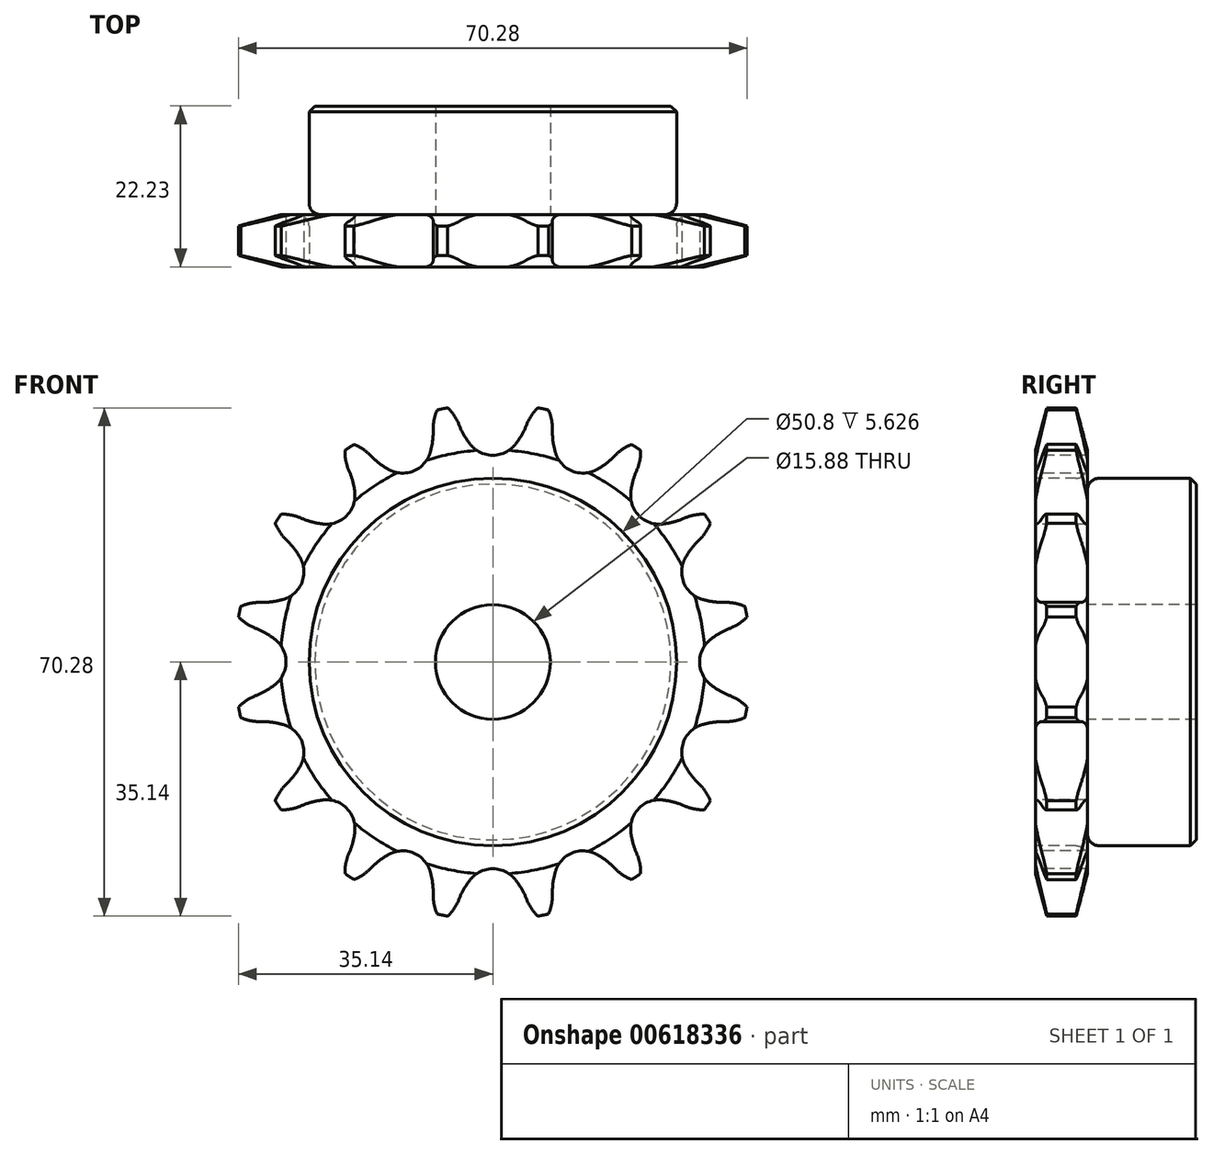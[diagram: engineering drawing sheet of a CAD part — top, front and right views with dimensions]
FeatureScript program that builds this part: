
annotation { "Feature Type Name" : "Feature", "Feature Type Description" : "" }
export const myFeature = defineFeature(function(context is Context, id is Id, definition is map)
    precondition{}
    {
        {
            var Q0;
            Q0=qCreatedBy(makeId("Right.planeOp"),FACE);
            var sketch = newSketch(context, id + "F0", { "sketchPlane" : qUnion([Q0])});
            skLineSegment(sketch, "E0", {"start": v(0, 0) * mm, "end": v(26.74, 0) * mm, "construction": true});
            skLineSegment(sketch, "E1.bottom", {"start": v(0, 7.94) * mm, "end": v(7.21, 7.94) * mm});
            skLineSegment(sketch, "E1.top", {"start": v(0, 35.69) * mm, "end": v(7.21, 35.69) * mm});
            skLineSegment(sketch, "E1.left", {"start": v(0, 7.94) * mm, "end": v(0, 35.69) * mm});
            skLineSegment(sketch, "E1.right", {"start": v(7.21, 7.94) * mm, "end": v(7.21, 35.69) * mm});
            skLineSegment(sketch, "E2.bottom", {"start": v(0, 7.94) * mm, "end": v(22.23, 7.94) * mm});
            skLineSegment(sketch, "E2.top", {"start": v(0, 25.4) * mm, "end": v(22.23, 25.4) * mm});
            skLineSegment(sketch, "E2.left", {"start": v(0, 7.94) * mm, "end": v(0, 25.4) * mm});
            skLineSegment(sketch, "E2.right", {"start": v(22.23, 7.94) * mm, "end": v(22.22, 25.4) * mm});
            skLineSegment(sketch, "E3.MirrorCS", {"start": v(0, -7.94) * mm, "end": v(7.21, -7.94) * mm});
            skLineSegment(sketch, "E4.MirrorCS", {"start": v(22.23, -7.94) * mm, "end": v(22.23, -25.4) * mm});
            skLineSegment(sketch, "E5.MirrorCS", {"start": v(0, -7.94) * mm, "end": v(0, -25.4) * mm});
            skLineSegment(sketch, "E6.MirrorCS", {"start": v(0, -35.69) * mm, "end": v(7.21, -35.69) * mm});
            skLineSegment(sketch, "E7.MirrorCS", {"start": v(0, -7.94) * mm, "end": v(0, -35.69) * mm});
            skLineSegment(sketch, "E8.MirrorCS", {"start": v(7.21, -7.94) * mm, "end": v(7.21, -35.69) * mm});
            skLineSegment(sketch, "E9.MirrorCS", {"start": v(0, -7.94) * mm, "end": v(22.23, -7.94) * mm});
            skLineSegment(sketch, "E10.MirrorCS", {"start": v(0, -25.4) * mm, "end": v(22.23, -25.4) * mm});
            skSolve(sketch);
        }
        {
            var Q0;
            {var subQ0=sQuery(id+"F0.wireOp",EDGE,"E1.top");Q0=makeQuery(id+"F0.imprint","IMPRINT",FACE,{"disambiguationData":[TD([[makeQuery(id+"F0.imprint","IMPRINT",EDGE,{"derivedFrom":subQ0}),-1.0]])]});}
            var Q1;
            {var subQ5=sQuery(id+"F0.wireOp",EDGE,"E2.left");Q1=makeQuery(id+"F0.imprint","IMPRINT",FACE,{"disambiguationData":[TD([[makeQuery(id+"F0.imprint","IMPRINT",EDGE,{"derivedFrom":subQ5}),-1.0]])]});}
            var Q2;
            {var subQ5=sQuery(id+"F0.wireOp",EDGE,"E2.right");Q2=makeQuery(id+"F0.imprint","IMPRINT",FACE,{"disambiguationData":[TD([[makeQuery(id+"F0.imprint","IMPRINT",EDGE,{"derivedFrom":subQ5}),1.0]])]});}
            var Q3;
            Q3=sQuery(id+"F0.wireOp",EDGE,"E0");
            revolve(context, id + "F1", {"entities" : qUnion([Q0, Q1, Q2]), "axis" : qUnion([Q3]), "revolveType" : RevolveType.FULL});
        }
        {
            var Q0;
            Q0=makeQuery(id+"F1.opRevolve","SWEPT_EDGE",EDGE,{"disambiguationData":[OSD([sQuery(id+"F0.wireOp",EDGE,"E1.right"),sQuery(id+"F0.wireOp",EDGE,"E2.top")])]});
            fillet(context, id + "F2", {"entities" : qUnion([Q0]), "radius" : 1.59 * mm, "tangentPropagation" : true, "allowEdgeOverflow" : false});
        }
        {
            var Q0;
            Q0=makeQuery(id+"F1.opRevolve","SWEPT_EDGE",EDGE,{"disambiguationData":[OSD([sQuery(id+"F0.wireOp",EDGE,"E2.top"),sQuery(id+"F0.wireOp",EDGE,"E2.right")])]});
            chamfer(context, id + "F3", {"entities" : qUnion([Q0]), "width" : 0.8 * mm, "tangentPropagation" : true});
        }
        {
            var Q0;
            Q0=makeQuery(id+"F1.opRevolve","SWEPT_FACE",FACE,{"disambiguationData":[OSD([sQuery(id+"F0.wireOp",EDGE,"E1.top")])]});
            chamfer(context, id + "F4", {"entities" : qUnion([Q0]), "chamferType" : ChamferType.TWO_OFFSETS, "width1" : 6.35 * mm, "oppositeDirection" : false, "width2" : 1.57 * mm, "tangentPropagation" : true});
        }
        {
            var Q0;
            Q0=makeQuery(id+"F1.opRevolve","SWEPT_FACE",FACE,{"disambiguationData":[OSD([sQuery(id+"F0.wireOp",EDGE,"E1.left"),sQuery(id+"F0.wireOp",EDGE,"E2.left")])]});
            var sketch = newSketch(context, id + "F5", { "sketchPlane" : qUnion([Q0])});
            skLineSegment(sketch, "E11", {"start": v(0, 0) * mm, "end": v(0, 32.55) * mm, "construction": true});
            skLineSegment(sketch, "E12", {"start": v(0, 32.55) * mm, "end": v(33.66, 32.55) * mm, "construction": true});
            skLineSegment(sketch, "E13", {"start": v(0, 32.55) * mm, "end": v(5, 36.56) * mm, "construction": true});
            skLineSegment(sketch, "E14", {"start": v(5, 36.56) * mm, "end": v(-3.9, 32.55) * mm, "construction": true});
            skLineSegment(sketch, "E15", {"start": v(3.62, 15.85) * mm, "end": v(-3.9, 32.55) * mm, "construction": true});
            skArc(sketch, "E16", {"start": v(-7.13, 35.87) * mm, "mid": v(-15.94, 26.26) * mm, "end": v(-4.66, 32.79) * mm, "construction": true});
            skArc(sketch, "E17", {"start": v(-4.66, 32.79) * mm, "mid": v(-5.66, 34.52) * mm, "end": v(-7.13, 35.87) * mm});
            skLineSegment(sketch, "E18", {"start": v(-4.66, 32.79) * mm, "end": v(-4.66, 32.79) * mm});
            skArc(sketch, "E19", {"start": v(-3.1, 30.07) * mm, "mid": v(-1.71, 28.98) * mm, "end": v(0, 28.59) * mm});
            skArc(sketch, "E20", {"start": v(-4.66, 32.79) * mm, "mid": v(-3.98, 31.37) * mm, "end": v(-3.1, 30.07) * mm});
            skArc(sketch, "E21.MirrorCS", {"start": v(4.66, 32.79) * mm, "mid": v(5.66, 34.52) * mm, "end": v(7.13, 35.87) * mm});
            skArc(sketch, "E22.MirrorCS", {"start": v(4.66, 32.79) * mm, "mid": v(3.98, 31.37) * mm, "end": v(3.1, 30.07) * mm});
            skArc(sketch, "E23.MirrorCS", {"start": v(3.1, 30.07) * mm, "mid": v(1.71, 28.98) * mm, "end": v(0, 28.59) * mm});
            skArc(sketch, "E24.1.0", {"start": v(-16.85, 28.5) * mm, "mid": v(-18.44, 29.72) * mm, "end": v(-20.32, 30.4) * mm});
            skArc(sketch, "E24.1.1", {"start": v(-16.85, 28.5) * mm, "mid": v(-15.68, 27.46) * mm, "end": v(-14.36, 26.6) * mm});
            skArc(sketch, "E24.1.2", {"start": v(-14.36, 26.6) * mm, "mid": v(-12.67, 26.12) * mm, "end": v(-10.94, 26.41) * mm});
            skArc(sketch, "E24.1.3", {"start": v(-8.65, 28.96) * mm, "mid": v(-9.5, 27.43) * mm, "end": v(-10.94, 26.41) * mm});
            skArc(sketch, "E24.1.4", {"start": v(-8.24, 32.08) * mm, "mid": v(-8.33, 30.5) * mm, "end": v(-8.65, 28.96) * mm});
            skArc(sketch, "E24.1.5", {"start": v(-8.24, 32.08) * mm, "mid": v(-7.98, 34.06) * mm, "end": v(-7.13, 35.87) * mm});
            skArc(sketch, "E24.2.0", {"start": v(-26.48, 19.89) * mm, "mid": v(-28.41, 20.4) * mm, "end": v(-30.4, 20.32) * mm});
            skArc(sketch, "E24.2.1", {"start": v(-26.48, 19.89) * mm, "mid": v(-25, 19.37) * mm, "end": v(-23.45, 19.08) * mm});
            skArc(sketch, "E24.2.2", {"start": v(-23.45, 19.08) * mm, "mid": v(-21.7, 19.28) * mm, "end": v(-20.21, 20.21) * mm});
            skArc(sketch, "E24.2.3", {"start": v(-19.08, 23.45) * mm, "mid": v(-19.28, 21.7) * mm, "end": v(-20.21, 20.21) * mm});
            skArc(sketch, "E24.2.4", {"start": v(-19.89, 26.48) * mm, "mid": v(-19.37, 25) * mm, "end": v(-19.08, 23.45) * mm});
            skArc(sketch, "E24.2.5", {"start": v(-19.89, 26.48) * mm, "mid": v(-20.4, 28.41) * mm, "end": v(-20.32, 30.4) * mm});
            skArc(sketch, "E24.3.0", {"start": v(-32.08, 8.24) * mm, "mid": v(-34.06, 7.98) * mm, "end": v(-35.87, 7.13) * mm});
            skArc(sketch, "E24.3.1", {"start": v(-32.08, 8.24) * mm, "mid": v(-30.5, 8.33) * mm, "end": v(-28.96, 8.65) * mm});
            skArc(sketch, "E24.3.2", {"start": v(-28.96, 8.65) * mm, "mid": v(-27.43, 9.5) * mm, "end": v(-26.41, 10.94) * mm});
            skArc(sketch, "E24.3.3", {"start": v(-26.6, 14.36) * mm, "mid": v(-26.12, 12.67) * mm, "end": v(-26.41, 10.94) * mm});
            skArc(sketch, "E24.3.4", {"start": v(-28.5, 16.85) * mm, "mid": v(-27.46, 15.68) * mm, "end": v(-26.6, 14.36) * mm});
            skArc(sketch, "E24.3.5", {"start": v(-28.5, 16.85) * mm, "mid": v(-29.72, 18.44) * mm, "end": v(-30.4, 20.32) * mm});
            skArc(sketch, "E24.4.0", {"start": v(-32.79, -4.66) * mm, "mid": v(-34.52, -5.66) * mm, "end": v(-35.87, -7.13) * mm});
            skArc(sketch, "E24.4.1", {"start": v(-32.79, -4.66) * mm, "mid": v(-31.37, -3.98) * mm, "end": v(-30.07, -3.1) * mm});
            skArc(sketch, "E24.4.2", {"start": v(-30.07, -3.1) * mm, "mid": v(-28.98, -1.71) * mm, "end": v(-28.59, 0) * mm});
            skArc(sketch, "E24.4.3", {"start": v(-30.07, 3.1) * mm, "mid": v(-28.98, 1.71) * mm, "end": v(-28.59, 0) * mm});
            skArc(sketch, "E24.4.4", {"start": v(-32.79, 4.66) * mm, "mid": v(-31.37, 3.98) * mm, "end": v(-30.07, 3.1) * mm});
            skArc(sketch, "E24.4.5", {"start": v(-32.79, 4.66) * mm, "mid": v(-34.52, 5.66) * mm, "end": v(-35.87, 7.13) * mm});
            skArc(sketch, "E24.5.0", {"start": v(-28.5, -16.85) * mm, "mid": v(-29.72, -18.44) * mm, "end": v(-30.4, -20.32) * mm});
            skArc(sketch, "E24.5.1", {"start": v(-28.5, -16.85) * mm, "mid": v(-27.46, -15.68) * mm, "end": v(-26.6, -14.36) * mm});
            skArc(sketch, "E24.5.2", {"start": v(-26.6, -14.36) * mm, "mid": v(-26.12, -12.67) * mm, "end": v(-26.41, -10.94) * mm});
            skArc(sketch, "E24.5.3", {"start": v(-28.96, -8.65) * mm, "mid": v(-27.43, -9.5) * mm, "end": v(-26.41, -10.94) * mm});
            skArc(sketch, "E24.5.4", {"start": v(-32.08, -8.24) * mm, "mid": v(-30.5, -8.33) * mm, "end": v(-28.96, -8.65) * mm});
            skArc(sketch, "E24.5.5", {"start": v(-32.08, -8.24) * mm, "mid": v(-34.06, -7.98) * mm, "end": v(-35.87, -7.13) * mm});
            skArc(sketch, "E24.6.0", {"start": v(-19.89, -26.48) * mm, "mid": v(-20.4, -28.41) * mm, "end": v(-20.32, -30.4) * mm});
            skArc(sketch, "E24.6.1", {"start": v(-19.89, -26.48) * mm, "mid": v(-19.37, -25) * mm, "end": v(-19.08, -23.45) * mm});
            skArc(sketch, "E24.6.2", {"start": v(-19.08, -23.45) * mm, "mid": v(-19.28, -21.7) * mm, "end": v(-20.21, -20.21) * mm});
            skArc(sketch, "E24.6.3", {"start": v(-23.45, -19.08) * mm, "mid": v(-21.7, -19.28) * mm, "end": v(-20.21, -20.21) * mm});
            skArc(sketch, "E24.6.4", {"start": v(-26.48, -19.89) * mm, "mid": v(-25, -19.37) * mm, "end": v(-23.45, -19.08) * mm});
            skArc(sketch, "E24.6.5", {"start": v(-26.48, -19.89) * mm, "mid": v(-28.41, -20.4) * mm, "end": v(-30.4, -20.32) * mm});
            skArc(sketch, "E24.7.0", {"start": v(-8.24, -32.08) * mm, "mid": v(-7.98, -34.06) * mm, "end": v(-7.13, -35.87) * mm});
            skArc(sketch, "E24.7.1", {"start": v(-8.24, -32.08) * mm, "mid": v(-8.33, -30.5) * mm, "end": v(-8.65, -28.96) * mm});
            skArc(sketch, "E24.7.2", {"start": v(-8.65, -28.96) * mm, "mid": v(-9.5, -27.43) * mm, "end": v(-10.94, -26.41) * mm});
            skArc(sketch, "E24.7.3", {"start": v(-14.36, -26.6) * mm, "mid": v(-12.67, -26.12) * mm, "end": v(-10.94, -26.41) * mm});
            skArc(sketch, "E24.7.4", {"start": v(-16.85, -28.5) * mm, "mid": v(-15.68, -27.46) * mm, "end": v(-14.36, -26.6) * mm});
            skArc(sketch, "E24.7.5", {"start": v(-16.85, -28.5) * mm, "mid": v(-18.44, -29.72) * mm, "end": v(-20.32, -30.4) * mm});
            skArc(sketch, "E24.8.0", {"start": v(4.66, -32.79) * mm, "mid": v(5.66, -34.52) * mm, "end": v(7.13, -35.87) * mm});
            skArc(sketch, "E24.8.1", {"start": v(4.66, -32.79) * mm, "mid": v(3.98, -31.37) * mm, "end": v(3.1, -30.07) * mm});
            skArc(sketch, "E24.8.2", {"start": v(3.1, -30.07) * mm, "mid": v(1.71, -28.98) * mm, "end": v(0, -28.59) * mm});
            skArc(sketch, "E24.8.3", {"start": v(-3.1, -30.07) * mm, "mid": v(-1.71, -28.98) * mm, "end": v(0, -28.59) * mm});
            skArc(sketch, "E24.8.4", {"start": v(-4.66, -32.79) * mm, "mid": v(-3.98, -31.37) * mm, "end": v(-3.1, -30.07) * mm});
            skArc(sketch, "E24.8.5", {"start": v(-4.66, -32.79) * mm, "mid": v(-5.66, -34.52) * mm, "end": v(-7.13, -35.87) * mm});
            skArc(sketch, "E24.9.0", {"start": v(16.85, -28.5) * mm, "mid": v(18.44, -29.72) * mm, "end": v(20.32, -30.4) * mm});
            skArc(sketch, "E24.9.1", {"start": v(16.85, -28.5) * mm, "mid": v(15.68, -27.46) * mm, "end": v(14.36, -26.6) * mm});
            skArc(sketch, "E24.9.2", {"start": v(14.36, -26.6) * mm, "mid": v(12.67, -26.12) * mm, "end": v(10.94, -26.41) * mm});
            skArc(sketch, "E24.9.3", {"start": v(8.65, -28.96) * mm, "mid": v(9.5, -27.43) * mm, "end": v(10.94, -26.41) * mm});
            skArc(sketch, "E24.9.4", {"start": v(8.24, -32.08) * mm, "mid": v(8.33, -30.5) * mm, "end": v(8.65, -28.96) * mm});
            skArc(sketch, "E24.9.5", {"start": v(8.24, -32.08) * mm, "mid": v(7.98, -34.06) * mm, "end": v(7.13, -35.87) * mm});
            skArc(sketch, "E24.10.0", {"start": v(26.48, -19.89) * mm, "mid": v(28.41, -20.4) * mm, "end": v(30.4, -20.32) * mm});
            skArc(sketch, "E24.10.1", {"start": v(26.48, -19.89) * mm, "mid": v(25, -19.37) * mm, "end": v(23.45, -19.08) * mm});
            skArc(sketch, "E24.10.2", {"start": v(23.45, -19.08) * mm, "mid": v(21.7, -19.28) * mm, "end": v(20.21, -20.21) * mm});
            skArc(sketch, "E24.10.3", {"start": v(19.08, -23.45) * mm, "mid": v(19.28, -21.7) * mm, "end": v(20.21, -20.21) * mm});
            skArc(sketch, "E24.10.4", {"start": v(19.89, -26.48) * mm, "mid": v(19.37, -25) * mm, "end": v(19.08, -23.45) * mm});
            skArc(sketch, "E24.10.5", {"start": v(19.89, -26.48) * mm, "mid": v(20.4, -28.41) * mm, "end": v(20.32, -30.4) * mm});
            skArc(sketch, "E24.11.0", {"start": v(32.08, -8.24) * mm, "mid": v(34.06, -7.98) * mm, "end": v(35.87, -7.13) * mm});
            skArc(sketch, "E24.11.1", {"start": v(32.08, -8.24) * mm, "mid": v(30.5, -8.33) * mm, "end": v(28.96, -8.65) * mm});
            skArc(sketch, "E24.11.2", {"start": v(28.96, -8.65) * mm, "mid": v(27.43, -9.5) * mm, "end": v(26.41, -10.94) * mm});
            skArc(sketch, "E24.11.3", {"start": v(26.6, -14.36) * mm, "mid": v(26.12, -12.67) * mm, "end": v(26.41, -10.94) * mm});
            skArc(sketch, "E24.11.4", {"start": v(28.5, -16.85) * mm, "mid": v(27.46, -15.68) * mm, "end": v(26.6, -14.36) * mm});
            skArc(sketch, "E24.11.5", {"start": v(28.5, -16.85) * mm, "mid": v(29.72, -18.44) * mm, "end": v(30.4, -20.32) * mm});
            skArc(sketch, "E24.12.0", {"start": v(32.79, 4.66) * mm, "mid": v(34.52, 5.66) * mm, "end": v(35.87, 7.13) * mm});
            skArc(sketch, "E24.12.1", {"start": v(32.79, 4.66) * mm, "mid": v(31.37, 3.98) * mm, "end": v(30.07, 3.1) * mm});
            skArc(sketch, "E24.12.2", {"start": v(30.07, 3.1) * mm, "mid": v(28.98, 1.71) * mm, "end": v(28.59, 0) * mm});
            skArc(sketch, "E24.12.3", {"start": v(30.07, -3.1) * mm, "mid": v(28.98, -1.71) * mm, "end": v(28.59, 0) * mm});
            skArc(sketch, "E24.12.4", {"start": v(32.79, -4.66) * mm, "mid": v(31.37, -3.98) * mm, "end": v(30.07, -3.1) * mm});
            skArc(sketch, "E24.12.5", {"start": v(32.79, -4.66) * mm, "mid": v(34.52, -5.66) * mm, "end": v(35.87, -7.13) * mm});
            skArc(sketch, "E24.13.0", {"start": v(28.5, 16.85) * mm, "mid": v(29.72, 18.44) * mm, "end": v(30.4, 20.32) * mm});
            skArc(sketch, "E24.13.1", {"start": v(28.5, 16.85) * mm, "mid": v(27.46, 15.68) * mm, "end": v(26.6, 14.36) * mm});
            skArc(sketch, "E24.13.2", {"start": v(26.6, 14.36) * mm, "mid": v(26.12, 12.67) * mm, "end": v(26.41, 10.94) * mm});
            skArc(sketch, "E24.13.3", {"start": v(28.96, 8.65) * mm, "mid": v(27.43, 9.5) * mm, "end": v(26.41, 10.94) * mm});
            skArc(sketch, "E24.13.4", {"start": v(32.08, 8.24) * mm, "mid": v(30.5, 8.33) * mm, "end": v(28.96, 8.65) * mm});
            skArc(sketch, "E24.13.5", {"start": v(32.08, 8.24) * mm, "mid": v(34.06, 7.98) * mm, "end": v(35.87, 7.13) * mm});
            skArc(sketch, "E24.14.0", {"start": v(19.89, 26.48) * mm, "mid": v(20.4, 28.41) * mm, "end": v(20.32, 30.4) * mm});
            skArc(sketch, "E24.14.1", {"start": v(19.89, 26.48) * mm, "mid": v(19.37, 25) * mm, "end": v(19.08, 23.45) * mm});
            skArc(sketch, "E24.14.2", {"start": v(19.08, 23.45) * mm, "mid": v(19.28, 21.7) * mm, "end": v(20.21, 20.21) * mm});
            skArc(sketch, "E24.14.3", {"start": v(23.45, 19.08) * mm, "mid": v(21.7, 19.28) * mm, "end": v(20.21, 20.21) * mm});
            skArc(sketch, "E24.14.4", {"start": v(26.48, 19.89) * mm, "mid": v(25, 19.37) * mm, "end": v(23.45, 19.08) * mm});
            skArc(sketch, "E24.14.5", {"start": v(26.48, 19.89) * mm, "mid": v(28.41, 20.4) * mm, "end": v(30.4, 20.32) * mm});
            skArc(sketch, "E24.15.0", {"start": v(8.24, 32.08) * mm, "mid": v(7.98, 34.06) * mm, "end": v(7.13, 35.87) * mm});
            skArc(sketch, "E24.15.1", {"start": v(8.24, 32.08) * mm, "mid": v(8.33, 30.5) * mm, "end": v(8.65, 28.96) * mm});
            skArc(sketch, "E24.15.2", {"start": v(8.65, 28.96) * mm, "mid": v(9.5, 27.43) * mm, "end": v(10.94, 26.41) * mm});
            skArc(sketch, "E24.15.3", {"start": v(14.36, 26.6) * mm, "mid": v(12.67, 26.12) * mm, "end": v(10.94, 26.41) * mm});
            skArc(sketch, "E24.15.4", {"start": v(16.85, 28.5) * mm, "mid": v(15.68, 27.46) * mm, "end": v(14.36, 26.6) * mm});
            skArc(sketch, "E24.15.5", {"start": v(16.85, 28.5) * mm, "mid": v(18.44, 29.72) * mm, "end": v(20.32, 30.4) * mm});
            skPoint(sketch, "E24.center", {"position": v(0, 0) * mm});
            skSolve(sketch);
        }
        {
            var Q0;
            Q0 = qSketchRegion(id + "F5", true);
            extrude(context, id + "F6", {"entities" : qUnion([Q0]), "operationType" : NewBodyOperationType.INTERSECT, "endBound" : BoundingType.THROUGH_ALL, "oppositeDirection" : true, "depth" : 25.4 * mm, "offsetDistance" : 25.4 * mm});
        }
    });
